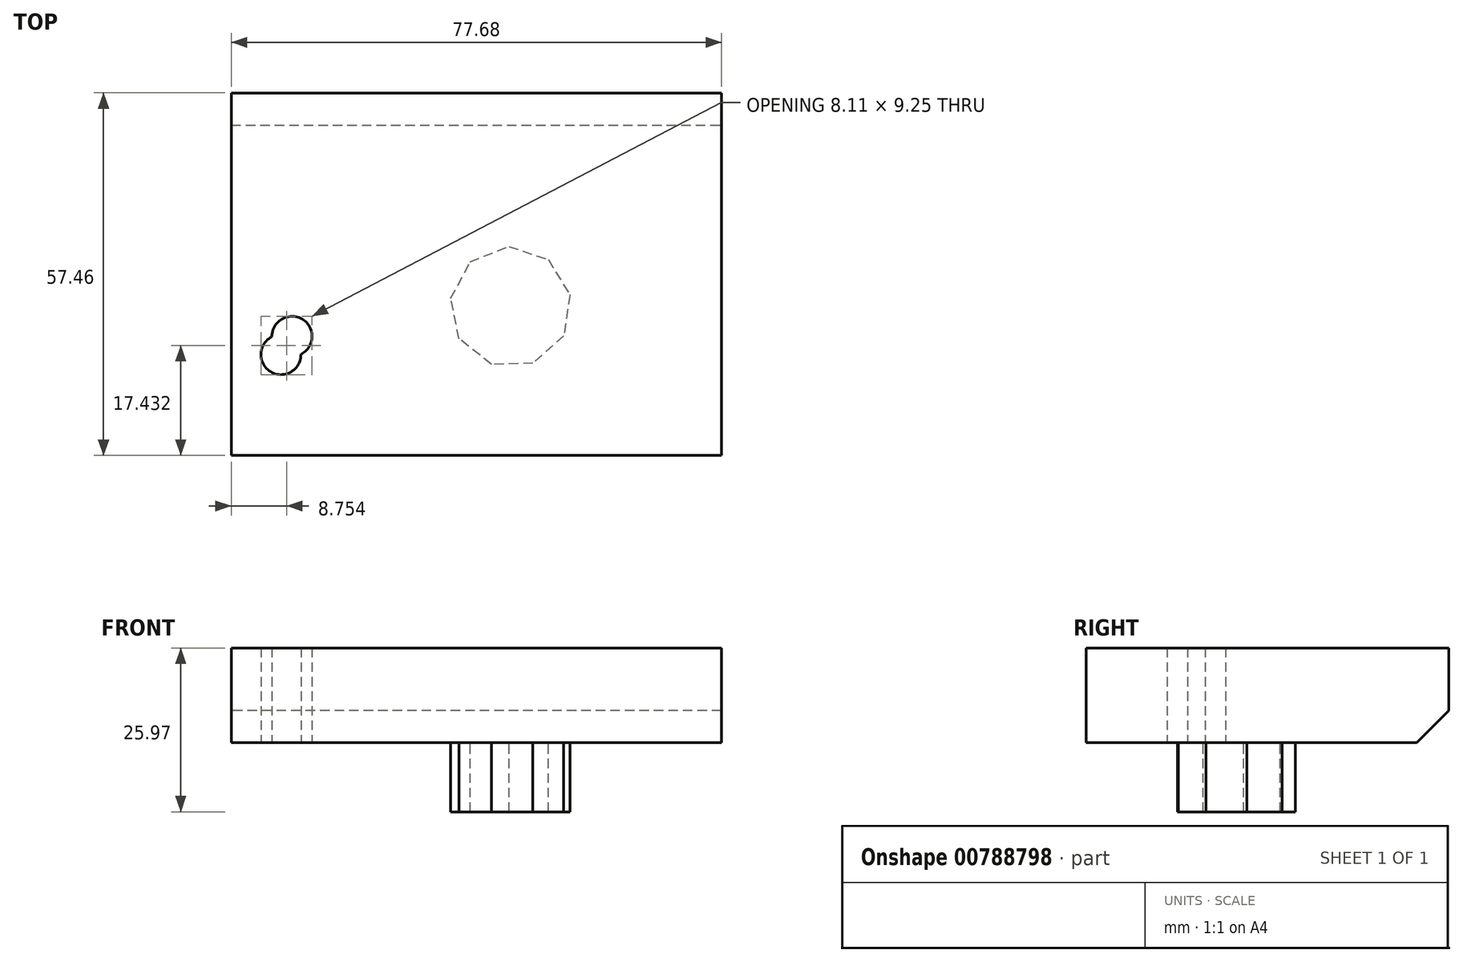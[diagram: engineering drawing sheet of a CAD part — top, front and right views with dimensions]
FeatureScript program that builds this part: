
annotation { "Feature Type Name" : "Feature", "Feature Type Description" : "" }
export const myFeature = defineFeature(function(context is Context, id is Id, definition is map)
    precondition{}
    {
        {
            var Q0;
            Q0=qCreatedBy(makeId("Top.planeOp"),FACE);
            var sketch = newSketch(context, id + "F0", { "sketchPlane" : qUnion([Q0])});
            skLineSegment(sketch, "E0.bottom", {"start": v(-34.7, -27.13) * mm, "end": v(42.97, -27.13) * mm});
            skLineSegment(sketch, "E0.top", {"start": v(-34.7, 30.33) * mm, "end": v(42.97, 30.33) * mm});
            skLineSegment(sketch, "E0.left", {"start": v(-34.7, -27.13) * mm, "end": v(-34.7, 30.33) * mm});
            skLineSegment(sketch, "E0.right", {"start": v(42.97, -27.13) * mm, "end": v(42.97, 30.33) * mm});
            skSolve(sketch);
        }
        {
            var Q0;
            Q0 = qSketchRegion(id + "F0", true);
            extrude(context, id + "F1", {"entities" : qUnion([Q0]), "depth" : 15 * mm, "offsetDistance" : 25.4 * mm});
        }
        {
            var Q0;
            Q0=makeQuery(id+"F1.opExtrude","CAP_EDGE",EDGE,{"disambiguationData":[OSD([sQuery(id+"F0.wireOp",EDGE,"E0.top")])],"isStart":true});
            chamfer(context, id + "F2", {"entities" : qUnion([Q0]), "width" : 5.08 * mm, "tangentPropagation" : true});
        }
        {
            var Q0;
            Q0=makeQuery(id+"F1.opExtrude","CAP_FACE",FACE,{"disambiguationData":[OSD([sQuery(id+"F0.wireOp",EDGE,"E0.bottom"),sQuery(id+"F0.wireOp",EDGE,"E0.top"),sQuery(id+"F0.wireOp",EDGE,"E0.left"),sQuery(id+"F0.wireOp",EDGE,"E0.right")])],"isStart":false});
            var sketch = newSketch(context, id + "F3", { "sketchPlane" : qUnion([Q0])});
            skSolve(sketch);
        }
        {
            var Q0;
            Q0=makeQuery(id+"F3.imprint","IMPRINT",FACE,{"disambiguationData":[TD([[makeQuery(id+"F3.imprint","IMPRINT",EDGE,{"derivedFrom":makeQuery(id+"F1.opExtrude","CAP_EDGE",EDGE,{"disambiguationData":[OSD([sQuery(id+"F0.wireOp",EDGE,"E0.bottom")])],"isStart":false})}),1.0]])]});
            var sketch = newSketch(context, id + "F4", { "sketchPlane" : qUnion([Q0])});
            skCircle(sketch, "E1.cCircle", {"center": v(9.55, -3.6) * mm, "radius": 9 * mm, "construction": true});
            skLineSegment(sketch, "E1.0", {"start": v(0.07, -2.2) * mm, "end": v(3.2, 3.57) * mm});
            skLineSegment(sketch, "E1.1", {"start": v(3.2, 3.57) * mm, "end": v(9.3, 5.98) * mm});
            skLineSegment(sketch, "E1.2", {"start": v(9.3, 5.98) * mm, "end": v(15.51, 3.91) * mm});
            skLineSegment(sketch, "E1.3", {"start": v(15.51, 3.91) * mm, "end": v(18.94, -1.68) * mm});
            skLineSegment(sketch, "E1.4", {"start": v(18.94, -1.68) * mm, "end": v(17.98, -8.16) * mm});
            skLineSegment(sketch, "E1.5", {"start": v(17.98, -8.16) * mm, "end": v(13.08, -12.51) * mm});
            skLineSegment(sketch, "E1.6", {"start": v(13.08, -12.51) * mm, "end": v(6.52, -12.7) * mm});
            skLineSegment(sketch, "E1.7", {"start": v(6.52, -12.7) * mm, "end": v(1.39, -8.62) * mm});
            skLineSegment(sketch, "E1.8", {"start": v(1.39, -8.62) * mm, "end": v(0.07, -2.2) * mm});
            skPoint(sketch, "E1.0.midPoint", {"position": v(1.63, 0.7) * mm});
            skSolve(sketch);
        }
        {
            var Q0;
            Q0 = qSketchRegion(id + "F4", true);
            var sketch = newSketch(context, id + "F5", { "sketchPlane" : qUnion([Q0])});
            skSolve(sketch);
        }
        {
            var Q0;
            Q0=makeQuery(id+"F5.imprint","IMPRINT",FACE,{"disambiguationData":[TD([[makeQuery(id+"F5.imprint","IMPRINT",EDGE,{"derivedFrom":makeQuery(id+"F4.imprint","IMPRINT",EDGE,{"derivedFrom":sQuery(id+"F4.wireOp",EDGE,"E1.0")})}),-1.0]])]});
            extrude(context, id + "F6", {"entities" : qUnion([Q0]), "operationType" : NewBodyOperationType.ADD, "oppositeDirection" : true, "depth" : 25.97 * mm, "offsetDistance" : 25.4 * mm});
        }
        {
            var Q0;
            Q0=makeQuery(id+"F1.opExtrude","CAP_FACE",FACE,{"disambiguationData":[OSD([sQuery(id+"F0.wireOp",EDGE,"E0.bottom"),sQuery(id+"F0.wireOp",EDGE,"E0.top"),sQuery(id+"F0.wireOp",EDGE,"E0.left"),sQuery(id+"F0.wireOp",EDGE,"E0.right")])],"isStart":true});
            var sketch = newSketch(context, id + "F7", { "sketchPlane" : qUnion([Q0])});
            skLineSegment(sketch, "E2.bottom", {"start": v(-25.08, 8.25) * mm, "end": v(-28.6, 8.25) * mm});
            skLineSegment(sketch, "E2.top", {"start": v(-25.08, 14.05) * mm, "end": v(-28.6, 14.05) * mm});
            skLineSegment(sketch, "E2.left", {"start": v(-25.08, 8.25) * mm, "end": v(-25.08, 14.05) * mm});
            skLineSegment(sketch, "E2.right", {"start": v(-28.6, 8.25) * mm, "end": v(-28.6, 14.05) * mm});
            skPoint(sketch, "E2.middle", {"position": v(-26.84, 11.15) * mm});
            skSolve(sketch);
        }
        {
            var Q0;
            Q0=sQuery(id+"F7.wireOp",VERTEX,"E2.left.start");
            var Q1;
            Q1=sQuery(id+"F7.wireOp",VERTEX,"E2.middle");
            var Q2;
            Q2=makeQuery(id+"F1.opExtrude","SWEPT_BODY",BODY,{"disambiguationData":[OSD([sQuery(id+"F0.wireOp",EDGE,"E0.bottom"),sQuery(id+"F0.wireOp",EDGE,"E0.top"),sQuery(id+"F0.wireOp",EDGE,"E0.left"),sQuery(id+"F0.wireOp",EDGE,"E0.right")])]});
            hole(context, id + "F8", {"style" : HoleStyle.SIMPLE, "endStyle" : HoleEndStyle.THROUGH, "holeDiameter" : 6.35 * mm, "majorDiameter" : 6.35 * mm, "isTappedThrough" : true, "tappedDepth" : 12.7 * mm, "tapClearance" : 3, "locations" : qUnion([Q0, Q1]), "scope" : qUnion([Q2])});
        }
    });
